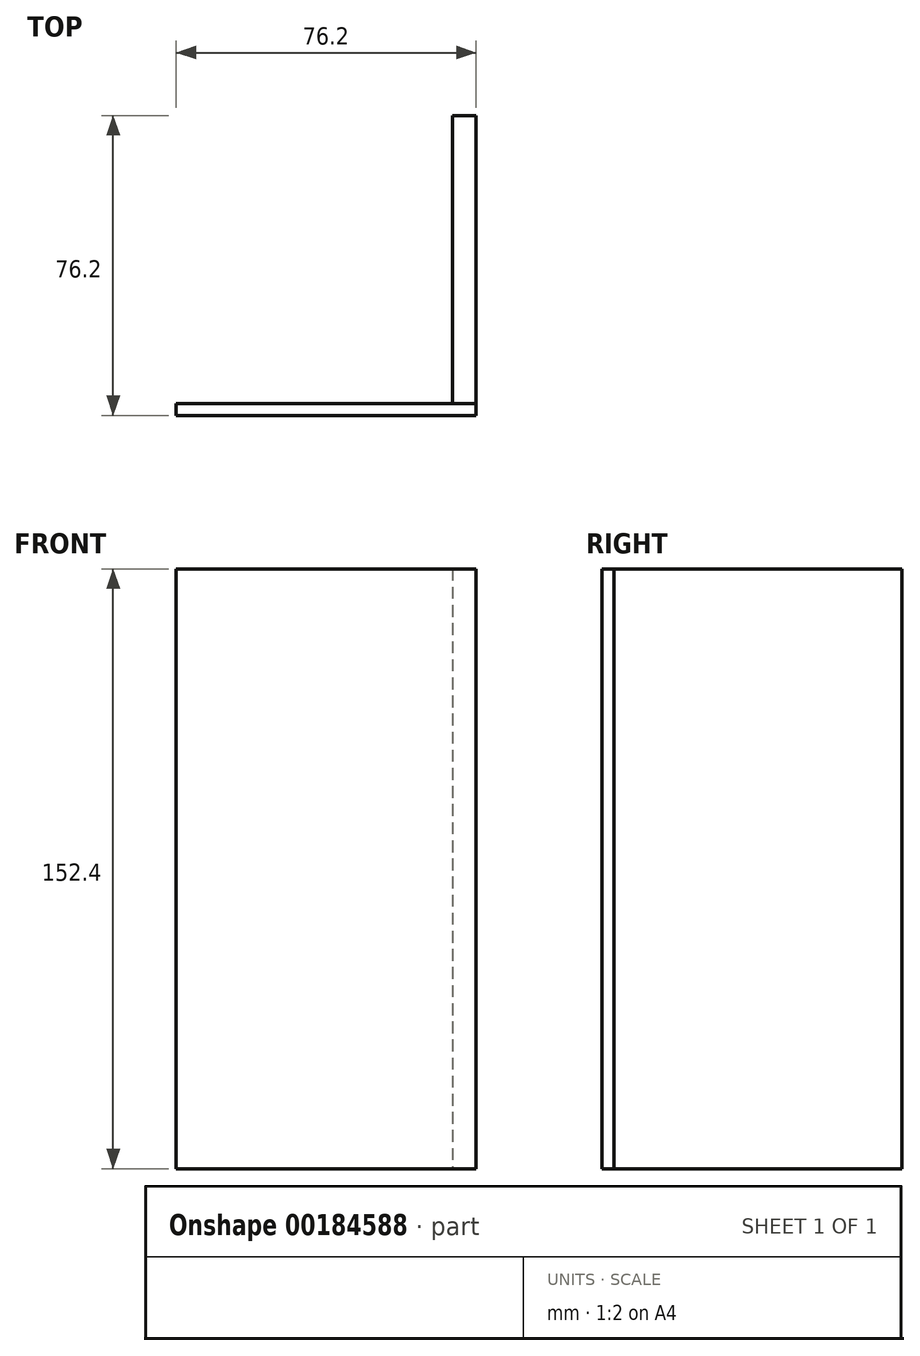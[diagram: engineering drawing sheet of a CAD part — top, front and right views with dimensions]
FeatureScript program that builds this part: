
annotation { "Feature Type Name" : "Feature", "Feature Type Description" : "" }
export const myFeature = defineFeature(function(context is Context, id is Id, definition is map)
    precondition{}
    {
        {
            var Q0;
            Q0=qCreatedBy(makeId("Top.planeOp"),FACE);
            var sketch = newSketch(context, id + "F0", { "sketchPlane" : qUnion([Q0])});
            skLineSegment(sketch, "E0.bottom", {"start": v(0, 0) * mm, "end": v(-76.2, 0) * mm});
            skLineSegment(sketch, "E0.top", {"start": v(0, 3) * mm, "end": v(-76.2, 3) * mm});
            skLineSegment(sketch, "E0.left", {"start": v(0, 0) * mm, "end": v(0, 3) * mm});
            skLineSegment(sketch, "E0.right", {"start": v(-76.2, 0) * mm, "end": v(-76.2, 3) * mm});
            skLineSegment(sketch, "E1.bottom", {"start": v(0, 0) * mm, "end": v(-6, 0) * mm});
            skLineSegment(sketch, "E1.top", {"start": v(0, 76.2) * mm, "end": v(-6, 76.2) * mm});
            skLineSegment(sketch, "E1.left", {"start": v(0, 0) * mm, "end": v(0, 76.2) * mm});
            skLineSegment(sketch, "E1.right", {"start": v(-6, 0) * mm, "end": v(-6, 76.2) * mm});
            skSolve(sketch);
        }
        {
            var Q0;
            {var subQ5=sQuery(id+"F0.wireOp",EDGE,"E1.bottom");Q0=makeQuery(id+"F0.imprint","IMPRINT",FACE,{"disambiguationData":[TD([[makeQuery(id+"F0.imprint","IMPRINT",EDGE,{"derivedFrom":subQ5}),-1.0]])]});}
            var Q1;
            {var subQ0=sQuery(id+"F0.wireOp",EDGE,"E0.bottom");Q1=makeQuery(id+"F0.imprint","IMPRINT",FACE,{"disambiguationData":[TD([[makeQuery(id+"F0.imprint","IMPRINT",EDGE,{"derivedFrom":subQ0}),-1.0]])]});}
            extrude(context, id + "F1", {"entities" : qUnion([Q0, Q1]), "depth" : 152.4 * mm});
        }
        {
            var Q0;
            {var subQ5=sQuery(id+"F0.wireOp",EDGE,"E1.top");Q0=makeQuery(id+"F0.imprint","IMPRINT",FACE,{"disambiguationData":[TD([[makeQuery(id+"F0.imprint","IMPRINT",EDGE,{"derivedFrom":subQ5}),1.0]])]});}
            var Q1;
            {var subQ5=sQuery(id+"F0.wireOp",EDGE,"E1.bottom");Q1=makeQuery(id+"F0.imprint","IMPRINT",FACE,{"disambiguationData":[TD([[makeQuery(id+"F0.imprint","IMPRINT",EDGE,{"derivedFrom":subQ5}),-1.0]])]});}
            extrude(context, id + "F2", {"entities" : qUnion([Q0, Q1]), "depth" : 152.4 * mm});
        }
    });
